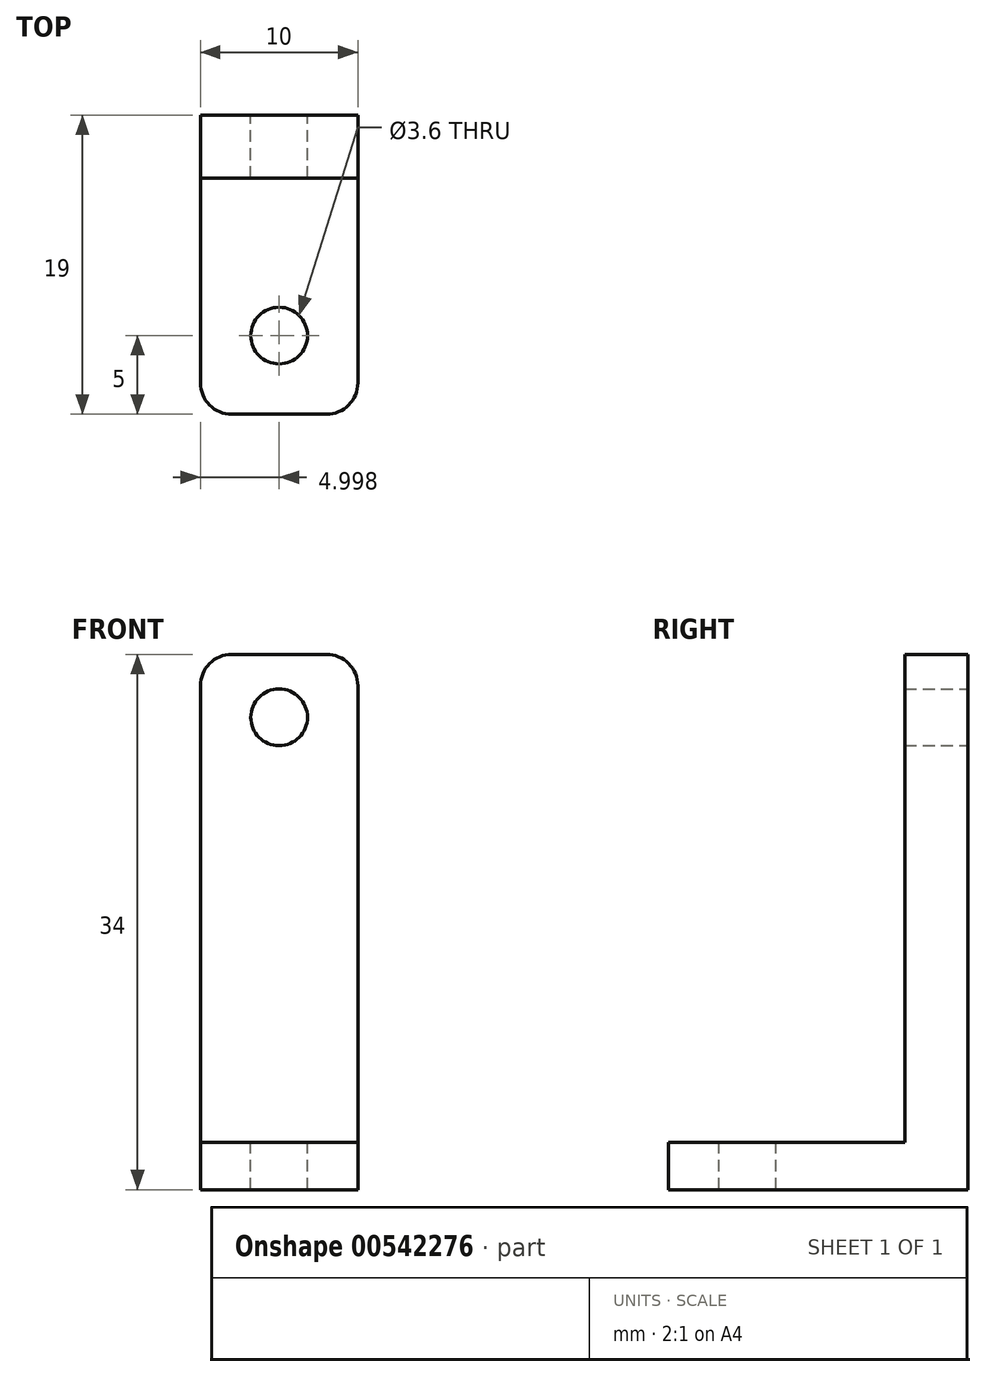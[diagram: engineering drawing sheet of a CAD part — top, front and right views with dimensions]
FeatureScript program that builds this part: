
annotation { "Feature Type Name" : "Feature", "Feature Type Description" : "" }
export const myFeature = defineFeature(function(context is Context, id is Id, definition is map)
    precondition{}
    {
        {
            var Q0;
            Q0=qCreatedBy(makeId("Front.planeOp"),FACE);
            var sketch = newSketch(context, id + "F0", { "sketchPlane" : qUnion([Q0])});
            skLineSegment(sketch, "E0.bottom", {"start": v(-4.5, 17.52) * mm, "end": v(5.5, 17.52) * mm});
            skLineSegment(sketch, "E0.top", {"start": v(-4.5, -16.48) * mm, "end": v(5.5, -16.48) * mm});
            skLineSegment(sketch, "E0.left", {"start": v(-4.5, 17.52) * mm, "end": v(-4.5, -16.48) * mm});
            skLineSegment(sketch, "E0.right", {"start": v(5.5, 17.52) * mm, "end": v(5.5, -16.48) * mm});
            skLineSegment(sketch, "E1", {"start": v(0.5, 17.52) * mm, "end": v(0.5, 13.52) * mm, "construction": true});
            skCircle(sketch, "E2", {"center": v(0.5, 13.52) * mm, "radius": 1.8 * mm});
            skLineSegment(sketch, "E3.bottom", {"start": v(5.5, -16.48) * mm, "end": v(-4.5, -16.48) * mm});
            skLineSegment(sketch, "E3.top", {"start": v(5.5, -13.48) * mm, "end": v(-4.5, -13.48) * mm});
            skLineSegment(sketch, "E3.left", {"start": v(5.5, -16.48) * mm, "end": v(5.5, -13.48) * mm});
            skLineSegment(sketch, "E3.right", {"start": v(-4.5, -16.48) * mm, "end": v(-4.5, -13.48) * mm});
            skSolve(sketch);
        }
        {
            var Q0;
            {var subQ1=sQuery(id+"F0.wireOp",EDGE,"E0.bottom");Q0=makeQuery(id+"F0.imprint","IMPRINT",FACE,{"disambiguationData":[TD([[makeQuery(id+"F0.imprint","IMPRINT",EDGE,{"derivedFrom":subQ1}),-1.0]])]});}
            extrude(context, id + "F1", {"entities" : qUnion([Q0]), "depth" : 4 * mm, "offsetDistance" : 25 * mm});
        }
        {
            var Q0;
            {var subQ0=sQuery(id+"F0.wireOp",EDGE,"E0.top");Q0=makeQuery(id+"F0.imprint","IMPRINT",FACE,{"disambiguationData":[TD([[makeQuery(id+"F0.imprint","IMPRINT",EDGE,{"derivedFrom":subQ0}),1.0]])]});}
            extrude(context, id + "F2", {"entities" : qUnion([Q0]), "operationType" : NewBodyOperationType.ADD, "depth" : 19 * mm, "offsetDistance" : 25 * mm});
        }
        {
            var Q0;
            Q0=makeQuery(id+"F2.opExtrude","SWEPT_FACE",FACE,{"disambiguationData":[OSD([sQuery(id+"F0.wireOp",EDGE,"E3.top")])]});
            var sketch = newSketch(context, id + "F3", { "sketchPlane" : qUnion([Q0])});
            skLineSegment(sketch, "E4", {"start": v(0.5, -4) * mm, "end": v(0.5, -14) * mm, "construction": true});
            skCircle(sketch, "E5", {"center": v(0.5, -14) * mm, "radius": 1.8 * mm});
            skSolve(sketch);
        }
        {
            var Q0;
            Q0=makeQuery(id+"F3.imprint","IMPRINT",FACE,{"disambiguationData":[TD([[makeQuery(id+"F3.imprint","IMPRINT",EDGE,{"derivedFrom":sQuery(id+"F3.wireOp",EDGE,"E5")}),1.0]])]});
            extrude(context, id + "F4", {"entities" : qUnion([Q0]), "operationType" : NewBodyOperationType.REMOVE, "oppositeDirection" : true, "depth" : 25 * mm, "offsetDistance" : 25 * mm});
        }
        {
            var Q0;
            Q0=makeQuery(id+"F1.opExtrude","SWEPT_EDGE",EDGE,{"disambiguationData":[OSD([sQuery(id+"F0.wireOp",EDGE,"E0.bottom"),sQuery(id+"F0.wireOp",EDGE,"E0.left")])]});
            var Q1;
            Q1=makeQuery(id+"F1.opExtrude","SWEPT_EDGE",EDGE,{"disambiguationData":[OSD([sQuery(id+"F0.wireOp",EDGE,"E0.bottom"),sQuery(id+"F0.wireOp",EDGE,"E0.right")])]});
            var Q2;
            Q2=makeQuery(id+"F2.opExtrude","CAP_EDGE",EDGE,{"disambiguationData":[OSD([sQuery(id+"F0.wireOp",EDGE,"E0.right")])],"isStart":false});
            var Q3;
            Q3=makeQuery(id+"F2.opExtrude","CAP_EDGE",EDGE,{"disambiguationData":[OSD([sQuery(id+"F0.wireOp",EDGE,"E0.left")])],"isStart":false});
            fillet(context, id + "F5", {"entities" : qUnion([Q0, Q1, Q2, Q3]), "radius" : 2 * mm, "tangentPropagation" : true, "allowEdgeOverflow" : false});
        }
    });
